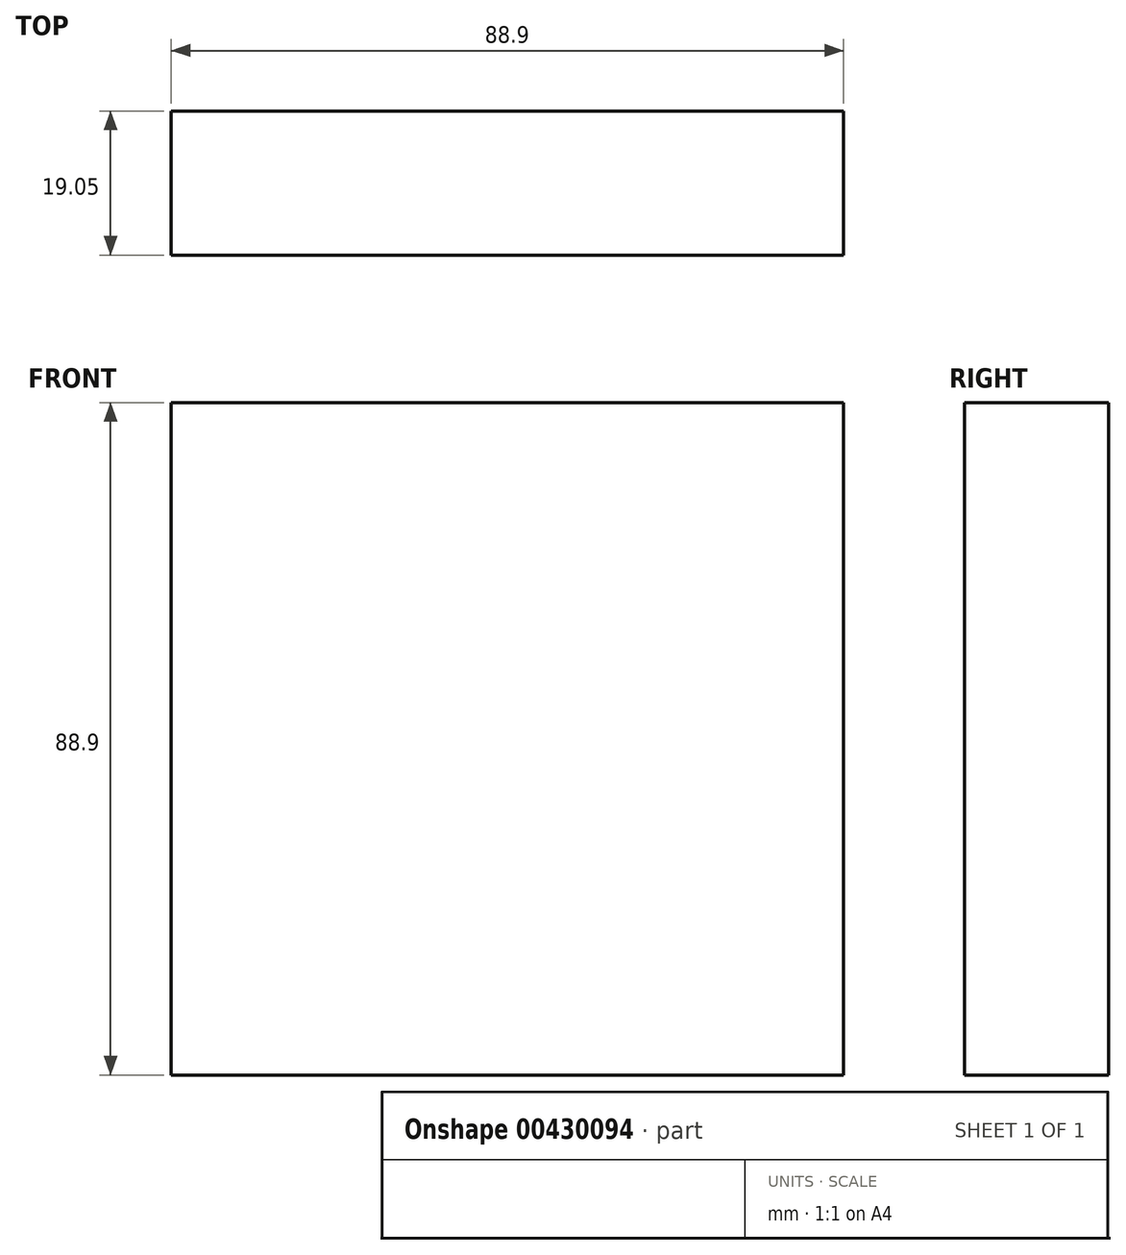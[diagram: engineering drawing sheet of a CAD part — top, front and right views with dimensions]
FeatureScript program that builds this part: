
annotation { "Feature Type Name" : "Feature", "Feature Type Description" : "" }
export const myFeature = defineFeature(function(context is Context, id is Id, definition is map)
    precondition{}
    {
        {
            var Q0;
            Q0=qCreatedBy(makeId("Top.planeOp"),FACE);
            var sketch = newSketch(context, id + "F0", { "sketchPlane" : qUnion([Q0])});
            skLineSegment(sketch, "E0.bottom", {"start": v(0, 0) * mm, "end": v(88.9, 0) * mm});
            skLineSegment(sketch, "E0.top", {"start": v(0, -19.05) * mm, "end": v(88.9, -19.05) * mm});
            skLineSegment(sketch, "E0.left", {"start": v(0, 0) * mm, "end": v(0, -19.05) * mm});
            skLineSegment(sketch, "E0.right", {"start": v(88.9, 0) * mm, "end": v(88.9, -19.05) * mm});
            skSolve(sketch);
        }
        {
            var Q0;
            Q0=makeQuery(id+"F0.imprint","IMPRINT",FACE,{"disambiguationData":[TD([[makeQuery(id+"F0.imprint","IMPRINT",EDGE,{"derivedFrom":sQuery(id+"F0.wireOp",EDGE,"E0.bottom")}),-1.0]])]});
            extrude(context, id + "F1", {"entities" : qUnion([Q0]), "depth" : 88.9 * mm});
        }
    });
